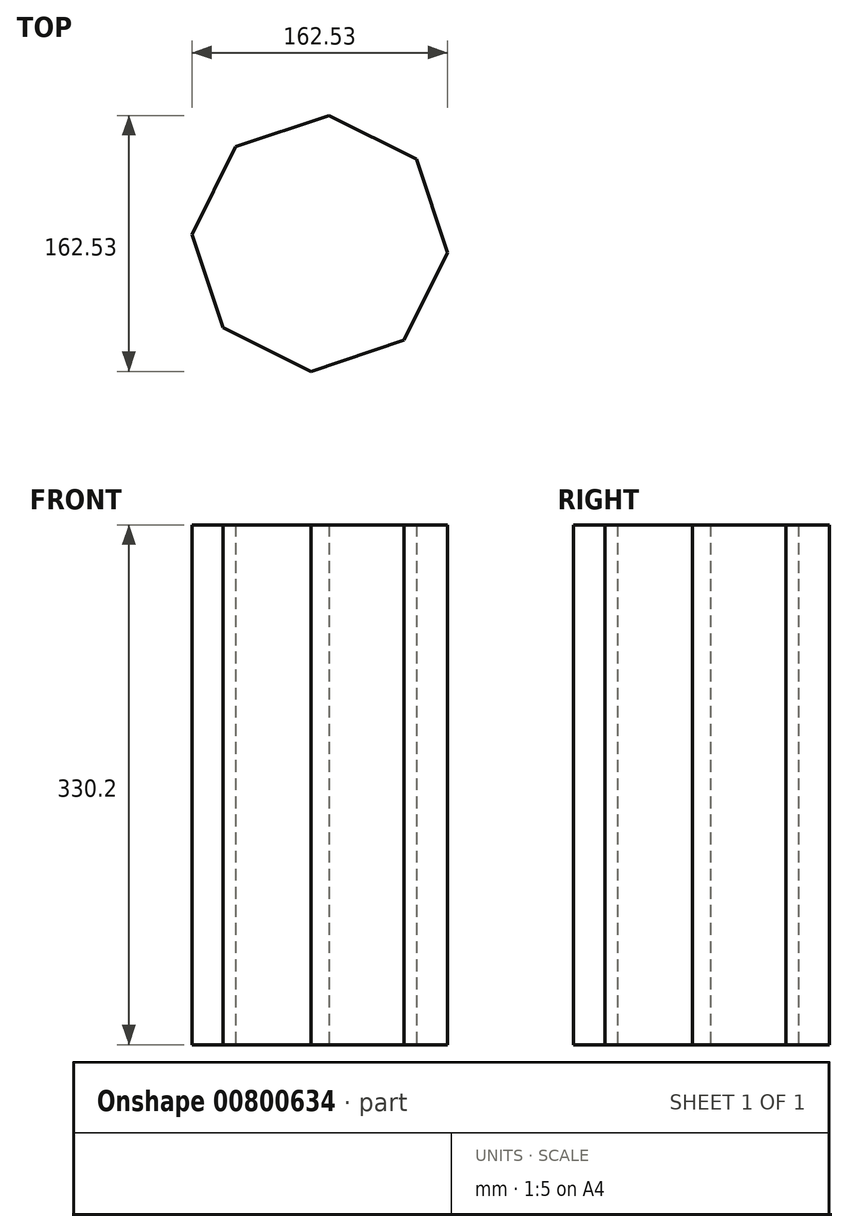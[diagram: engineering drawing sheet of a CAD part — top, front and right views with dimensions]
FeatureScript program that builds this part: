
annotation { "Feature Type Name" : "Feature", "Feature Type Description" : "" }
export const myFeature = defineFeature(function(context is Context, id is Id, definition is map)
    precondition{}
    {
        {
            var Q0;
            Q0=qCreatedBy(makeId("Top.planeOp"),FACE);
            var sketch = newSketch(context, id + "F0", { "sketchPlane" : qUnion([Q0])});
            skCircle(sketch, "E0.cCircle", {"center": v(16.81, -71.39) * mm, "radius": 75.27 * mm, "construction": true});
            skLineSegment(sketch, "E0.0", {"start": v(-36.6, -9.88) * mm, "end": v(22.54, 9.88) * mm});
            skLineSegment(sketch, "E0.1", {"start": v(22.54, 9.88) * mm, "end": v(78.33, -17.97) * mm});
            skLineSegment(sketch, "E0.2", {"start": v(78.33, -17.97) * mm, "end": v(98.08, -77.11) * mm});
            skLineSegment(sketch, "E0.3", {"start": v(98.08, -77.11) * mm, "end": v(70.23, -132.9) * mm});
            skLineSegment(sketch, "E0.4", {"start": v(70.23, -132.9) * mm, "end": v(11.09, -152.65) * mm});
            skLineSegment(sketch, "E0.5", {"start": v(11.09, -152.65) * mm, "end": v(-44.7, -124.8) * mm});
            skLineSegment(sketch, "E0.6", {"start": v(-44.7, -124.8) * mm, "end": v(-64.45, -65.66) * mm});
            skLineSegment(sketch, "E0.7", {"start": v(-64.45, -65.66) * mm, "end": v(-36.6, -9.88) * mm});
            skPoint(sketch, "E0.0.midPoint", {"position": v(-7.03, 0) * mm});
            skSolve(sketch);
        }
        {
            var Q0;
            Q0=makeQuery(id+"F0.imprint","IMPRINT",FACE,{"disambiguationData":[TD([[makeQuery(id+"F0.imprint","IMPRINT",EDGE,{"derivedFrom":sQuery(id+"F0.wireOp",EDGE,"E0.0")}),-1.0]])]});
            extrude(context, id + "F1", {"entities" : qUnion([Q0]), "depth" : 330.2 * mm, "offsetDistance" : 25.4 * mm});
        }
    });
